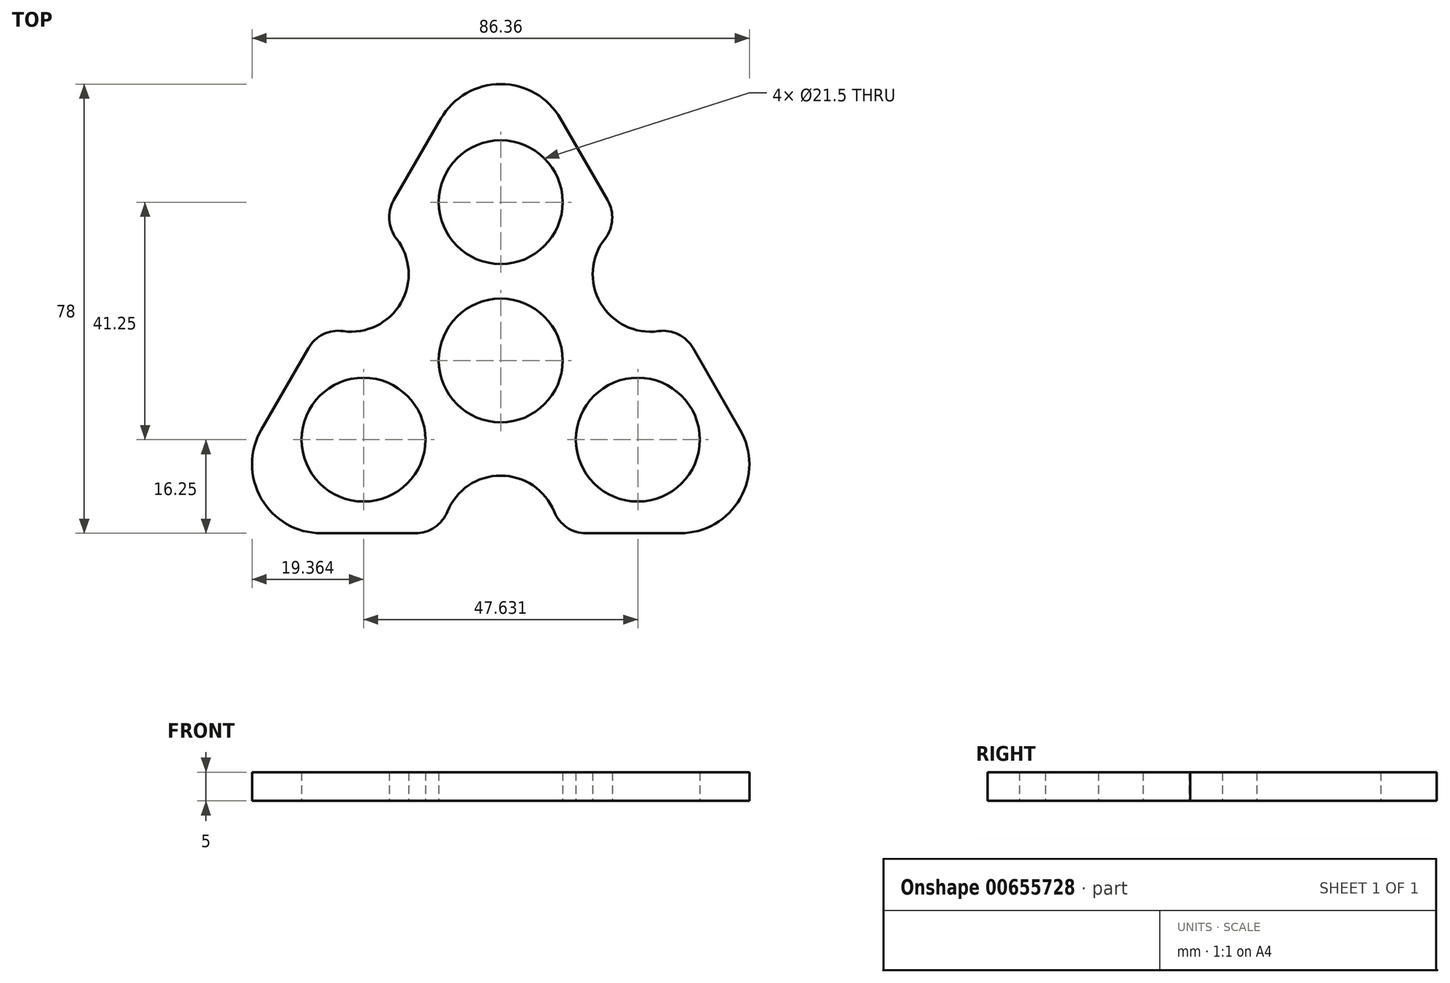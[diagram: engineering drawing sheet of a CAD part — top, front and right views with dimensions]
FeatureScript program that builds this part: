
annotation { "Feature Type Name" : "Feature", "Feature Type Description" : "" }
export const myFeature = defineFeature(function(context is Context, id is Id, definition is map)
    precondition{}
    {
        {
            var Q0;
            Q0=qCreatedBy(makeId("Top.planeOp"),FACE);
            var sketch = newSketch(context, id + "F0", { "sketchPlane" : qUnion([Q0])});
            skCircle(sketch, "E0", {"center": v(0, 0) * mm, "radius": 10.75 * mm});
            skCircle(sketch, "E1", {"center": v(0, 0) * mm, "radius": 27.5 * mm, "construction": true});
            skLineSegment(sketch, "E2", {"start": v(0, 0) * mm, "end": v(0, 27.5) * mm, "construction": true});
            skCircle(sketch, "E3", {"center": v(0, 27.5) * mm, "radius": 10.75 * mm});
            skCircle(sketch, "E4.1.0", {"center": v(23.82, -13.75) * mm, "radius": 10.75 * mm});
            skCircle(sketch, "E4.2.0", {"center": v(-23.82, -13.75) * mm, "radius": 10.75 * mm});
            skLineSegment(sketch, "E4.anchor1", {"start": v(0, 27.5) * mm, "end": v(0, 0) * mm, "construction": true});
            skLineSegment(sketch, "E4.anchor2", {"start": v(-23.82, -13.75) * mm, "end": v(0, 0) * mm, "construction": true});
            skCircle(sketch, "E5", {"center": v(0, 0) * mm, "radius": 30 * mm, "construction": true});
            skLineSegment(sketch, "E6", {"start": v(-51.96, -30) * mm, "end": v(51.96, -30) * mm, "construction": true});
            skLineSegment(sketch, "E7", {"start": v(51.96, -30) * mm, "end": v(0, 60) * mm, "construction": true});
            skLineSegment(sketch, "E8", {"start": v(0, 60) * mm, "end": v(-51.96, -30) * mm, "construction": true});
            skLineSegment(sketch, "E9", {"start": v(9.3, 5.37) * mm, "end": v(-33.13, -19.12) * mm, "construction": true});
            skLineSegment(sketch, "E10", {"start": v(9.3, 5.37) * mm, "end": v(0, 0) * mm, "construction": true});
            skArc(sketch, "E11", {"start": v(10, -30) * mm, "mid": v(0, -20) * mm, "end": v(-10, -30) * mm});
            skLineSegment(sketch, "E12", {"start": v(-10, -30) * mm, "end": v(-51.96, -30) * mm});
            skLineSegment(sketch, "E13", {"start": v(10, -30) * mm, "end": v(51.96, -30) * mm});
            skArc(sketch, "E14.1.0", {"start": v(20.98, 23.66) * mm, "mid": v(17.32, 10) * mm, "end": v(30.98, 6.34) * mm});
            skLineSegment(sketch, "E14.1.1", {"start": v(30.98, 6.34) * mm, "end": v(51.96, -30) * mm});
            skLineSegment(sketch, "E14.1.2", {"start": v(20.98, 23.66) * mm, "end": v(0, 60) * mm});
            skArc(sketch, "E14.2.0", {"start": v(-30.98, 6.34) * mm, "mid": v(-17.32, 10) * mm, "end": v(-20.98, 23.66) * mm});
            skLineSegment(sketch, "E14.2.1", {"start": v(-20.98, 23.66) * mm, "end": v(0, 60) * mm});
            skLineSegment(sketch, "E14.2.2", {"start": v(-30.98, 6.34) * mm, "end": v(-51.96, -30) * mm});
            skSolve(sketch);
        }
        {
            var Q0;
            Q0=makeQuery(id+"F0.imprint","IMPRINT",FACE,{"disambiguationData":[TD([[makeQuery(id+"F0.imprint","IMPRINT",EDGE,{"derivedFrom":sQuery(id+"F0.wireOp",EDGE,"E0")}),-1.0]])]});
            extrude(context, id + "F1", {"entities" : qUnion([Q0]), "depth" : 5 * mm, "offsetDistance" : 25 * mm});
        }
        {
            var Q0;
            Q0=makeQuery(id+"F1.opExtrude","SWEPT_EDGE",EDGE,{"disambiguationData":[OSD([sQuery(id+"F0.wireOp",EDGE,"E12"),sQuery(id+"F0.wireOp",EDGE,"E14.2.2")])]});
            var Q1;
            Q1=makeQuery(id+"F1.opExtrude","SWEPT_EDGE",EDGE,{"disambiguationData":[OSD([sQuery(id+"F0.wireOp",EDGE,"E13"),sQuery(id+"F0.wireOp",EDGE,"E14.1.1")])]});
            var Q2;
            Q2=makeQuery(id+"F1.opExtrude","SWEPT_EDGE",EDGE,{"disambiguationData":[OSD([sQuery(id+"F0.wireOp",EDGE,"E14.1.2"),sQuery(id+"F0.wireOp",EDGE,"E14.2.1")])]});
            fillet(context, id + "F2", {"entities" : qUnion([Q0, Q1, Q2]), "radius" : 12 * mm, "tangentPropagation" : true, "allowEdgeOverflow" : false});
        }
        {
            var Q0;
            Q0=makeQuery(id+"F1.opExtrude","SWEPT_EDGE",EDGE,{"disambiguationData":[OSD([sQuery(id+"F0.wireOp",EDGE,"E14.1.0"),sQuery(id+"F0.wireOp",EDGE,"E14.1.1")])]});
            var Q1;
            Q1=makeQuery(id+"F1.opExtrude","SWEPT_EDGE",EDGE,{"disambiguationData":[OSD([sQuery(id+"F0.wireOp",EDGE,"E14.1.0"),sQuery(id+"F0.wireOp",EDGE,"E14.1.2")])]});
            var Q2;
            Q2=makeQuery(id+"F1.opExtrude","SWEPT_EDGE",EDGE,{"disambiguationData":[OSD([sQuery(id+"F0.wireOp",EDGE,"E14.2.0"),sQuery(id+"F0.wireOp",EDGE,"E14.2.1")])]});
            var Q3;
            Q3=makeQuery(id+"F1.opExtrude","SWEPT_EDGE",EDGE,{"disambiguationData":[OSD([sQuery(id+"F0.wireOp",EDGE,"E14.2.0"),sQuery(id+"F0.wireOp",EDGE,"E14.2.2")])]});
            var Q4;
            Q4=makeQuery(id+"F1.opExtrude","SWEPT_EDGE",EDGE,{"disambiguationData":[OSD([sQuery(id+"F0.wireOp",EDGE,"E11"),sQuery(id+"F0.wireOp",EDGE,"E12")])]});
            var Q5;
            Q5=makeQuery(id+"F1.opExtrude","SWEPT_EDGE",EDGE,{"disambiguationData":[OSD([sQuery(id+"F0.wireOp",EDGE,"E11"),sQuery(id+"F0.wireOp",EDGE,"E13")])]});
            fillet(context, id + "F3", {"entities" : qUnion([Q0, Q1, Q2, Q3, Q4, Q5]), "radius" : 6 * mm, "tangentPropagation" : true, "allowEdgeOverflow" : false});
        }
    });
